# Revit family: EL817
name_source: partatom
category: Lighting Fixtures
revit_build: Autodesk Revit 2013 (Build: 20120221_2030(x64)
units: mm (PartAtom-declared; Revit-internal decimal feet)

## types (6) — shared parameters
Apparent Load = 0 VA
Backbox = Hubbell-Black
Color Filter = 16777215
Color Option = KL retrofit : Black
Default Elevation = 48 "
Description = Step Light Round
Dimming Lamp Color Temperature Shift = <None>
Emit Shape Visible in Rendering = No
Emit from Circle Diameter = 4 "
Glass = Hubbell-White Glass
Load Classification = Lighting
Manufacturer = KIM Lighting
Manufacturer Fax = 626-369-2695
Model = EL817
Photometric Link = http://www.kimlighting.com
Power factor = 1
Product Documentation Link = http://www.kimlighting.com
Product Page URL = http://www.kimlighting.com
Tilt Angle = 90.00°
URL = http://www.kimlighting.com
Voltage = 120 V
Wattage Comments = 5-10 W

## per-type parameters (varying)
| type | Lamp | Photometric Web File | Watt | zz Angle |
| EL817-3L-3K | 3 LED | el817-3l3k.ies | 10 W | 179.00° |
| EL817-3L-4k | 3 LED | el817-3l4k.ies | 5 W | 179.00° |
| EL817-3L-5k | 3 LED | el817-3l5k.ies | 5 W | 179.00° |
| EL817-9L-3k | 9 LED | el817-9l3k.ies | 10 W | 89.00° |
| EL817-9L-4K | 9 LED | el817-9l4k.ies | 10 W | 89.00° |
| EL817-9L-5K | 9 LED | el817-9l5k.ies | 10 W | 89.00° |

## geometry (parser evidence)
native form markers: Blend x25, Sweep x3
no freeform markers — native parametric forms only
